# Revit family: Deca_Misturador monocomando de mesa para cozinha_Gourmet_2280
name_source: partatom
category: Plumbing Fixtures
units: mm (PartAtom-declared; Revit-internal decimal feet)

## family parameters
Cut with Voids When Loaded = No
Host = Face
Part Type = Normal
Room Calculation Point = No
Round Connector Dimension = Use Radius
Shared = No

## types (4) — shared parameters
Acompanha o Produto = Acompanha Ligação Flexivel
Aprovado por = quattroD
Atendimento ao Cliente = 0800-0117073
Categoria = METAIS PARA COZINHA
Composição Anel Vedação = -
Composição Assento = -
Composição Básica = Liga de Cobre (bronze e latão),Plásticos de Engenharia,Elastômeros
Composição Componente = -
Consumo = -
Cor Interna = -
Cor Secundária = -
Cores Componente = -
Criado por = quattroD
Código Pai = 2280
Description = Misturador monocomando de mesa para cozinha
Diâmetro Água Fria = 15 mm  [stored 0.0492126 ft]
Diâmetro Água Quente = 15 mm  [stored 0.0492126 ft]
Informações Complementares = -
Itens de Instalação = -
Linha = Gourmet
Manufacturer = Deca
Norma = Não Possui
Pressão máx. funcionamento = 40 MCA
Pressão mín. Aquec. Acúmulo = 10 MCA
Pressão mín. Aquec. Passagem = 18 MCA
Pressão mín. funcionamento = 10 MCA
Raio Água Fria = 8 mm  [stored 0.0262467 ft]
Raio Água Quente = 8 mm  [stored 0.0262467 ft]
Saída de Esgoto = -
Segmento = Banheiro Luxo
Tipo de dispositivo economizador = Não
Tipo de mecanismo utilizado = Cartucho Monocomando
Tipo de rosca de entrada = BSP NBR 8133
Tipo de rosca de saída = -
URL = www.deca.com.br
Vazão na Pressão máx. (L/min) = 16
Vazão na Pressão mín. (L/min) = 4
zero-valued in all types: CWFU, Default Elevation, HWFU, WFU

## per-type parameters (varying)
| type | Cor Principal | Material | Model | Peso Líquido (Kg) |
| 2280.C_Cromado | Cromado | Deca_Cromado | 2280.C | 5.252 |
| 2280.GL.RD_Red Gold | Red Gold | Deca_Red Gold | 2280.GL.RD | 5.251 |
| 2280.BL.MT_Black Matte | Black Matte | Deca_Black Matte | 2280.BL.MT | 5.251 |
| 2280.CT.MT_Corten | Corten | Deca_Corten | 2280.CT.MT | 5.251 |

note: source unit labels omitted for Vazão na Pressão máx. (L/min), Vazão na Pressão mín. (L/min) — the stored unit's dimension contradicts the parameter name (converter mislabeling)

note: [stored X ft] marks values corroborated as IEEE doubles in the binary element streams (Revit-internal decimal feet)

## geometry (parser evidence)
native form markers: Sweep x1
no freeform markers — native parametric forms only
